# Revit family: IS_StradaO_K0795_BIM_DE
name_source: partatom
category: Plumbing Fixtures
revit_build: Autodesk Revit MEP 2016 (Build: 20161004_0715(x64)
units: mm (PartAtom-declared; Revit-internal decimal feet)

## family parameters
Always vertical = No
Cut with Voids When Loaded = No
OmniClass Number = 23.45.05.14.14
OmniClass Title = Sinks/Lavatories
Part Type = Normal
Room Calculation Point = No
Round Connector Dimension = Use Diameter
Shared = No
Work Plane-Based = No

## types (2) — shared parameters
Accessories = www.idealstandard.de\ersatzteile
AssetType = Fixed
BIMobject category = Basins
BOSUseNativeGeometries = 1
Brand = Ideal Standard
Brand url = http://www.idealstandard.de
CodePerformance = DIN EN 14688 CL 00, DIN EN 31
ConnectionType = Plumbing
CurrencyUnit = €
CurrentRevision = 1
DurationUnit = Jaar
EAN code = https://4015413041997
Edition number = 1
ExpectedLife = 25
Features = STRADA O vessel basin 410x410mm, no taphole, no overflow
IFC Classification = Sanitary Terminal
IfcExportAs = Sanitary terminal type
IfcExportType = WASHBASIN
Installation instructions = http://www.idealstandard.de
InstallationInstructions = www.idealstandard.de\produkte
LinearUnits = millimetres
MaintenanceInformation = www.idealstandard.de
Manufacturer = http://www.idealstandard.de
Manufacturer name = Ideal Standard
ManufacturerURL = http://www.idealstandard.de
Material = Vitreous china
Material main = Ceramics
NettWeight = 8,2 kg
Nominal height = 150
Nominal width = 410
NominalHeight = 155 mm
NominalLength = 412 mm
NominalWidth = 412 mm
Product Guid = d2c5c755-d180-4606-a00f-871fdb356574
Product SKU = K0795
Product certification = DIN EN 14688 CL 00, DIN EN 31
Product data url = https://bimobject.com
Product family = STRADA O
Product group = Basin
Product name = STRADA O vessel basin 410x410mm, no taphole, no overflow
Product url = http://www.idealstandard.de
ProductInformation = www.idealstandard.de/produkte
QR code = http://bimobject.com
Shape = Sculptured
Size = 412x412x155 mm
Space = Internal
SpareParts = www.idealstandard.de/ersatzteile
Technical description = http://www.idealstandard.de
URL = http://www.idealstandard.de
Uniclass2015Code = Pr_40_20_96_18
Uniclass2015Title = Counter top wash basins
Uniclass2015Version = Products v1.1
VolumeUnits = Litres
WashHandBasinMounting = Countertop
WashHandBasinType = Hand Rinse
Weight Net (Kg) = 8.2
zero-valued in all types: Cost, DrainSize

## per-type parameters (varying)
| type | BIMObjectName | BarCode | Color | Finish | MainColor | Model | ModelNumber | Name |
| K079501 STRADA O vessel basin 410x410mm, no taphole, no overflow | ISI_IdealStandard_CounterTopWashbasins_STRADA_K079501 | 4015413041997 | White | White | White | K079501 | K079501 | ISI_IdealStandard_CounterTopWashbasins_STRADA_K079501 |
| K0795MA STRADA O vessel basin 410x410mm, no taphole, no overflow | ISI_IdealStandard_CounterTopWashbasins_STRADA_K0795MA | 4015413042000 | WHITE IP | WHITE IP | WHITE IP | K0795MA | K0795MA | ISI_IdealStandard_CounterTopWashbasins_STRADA_K0795MA |

note: column(s) folded — value = type name in every type: Description, ModelReference

## geometry (parser evidence)
native form markers: Blend x4, Sweep x1
no freeform markers — native parametric forms only
